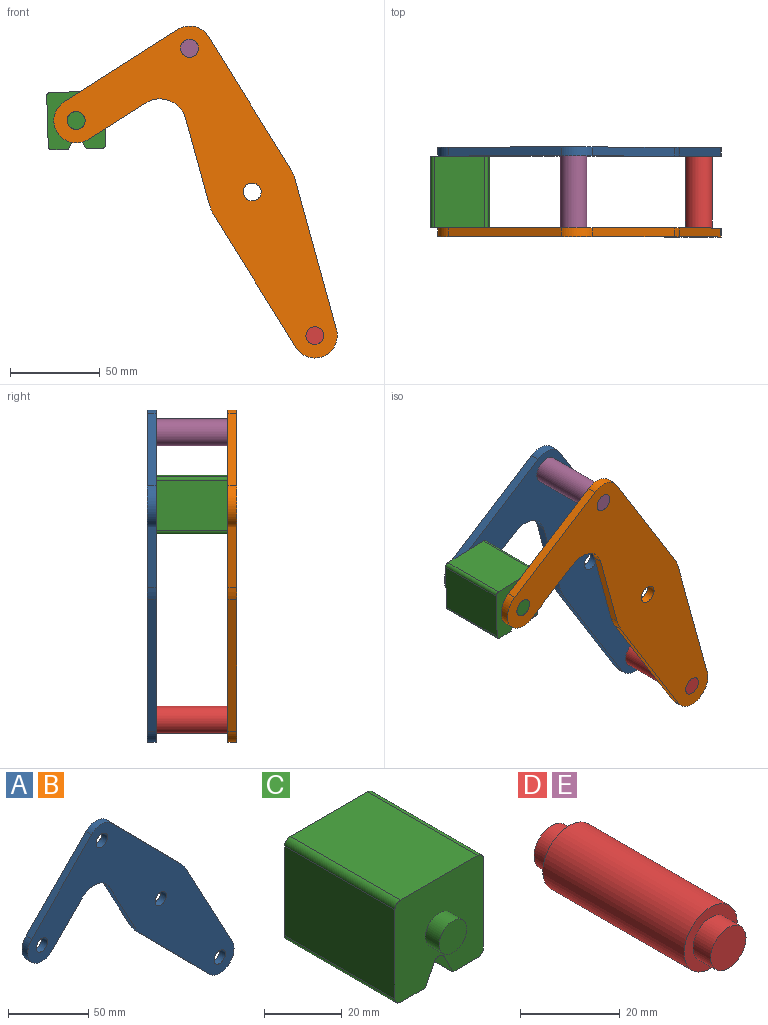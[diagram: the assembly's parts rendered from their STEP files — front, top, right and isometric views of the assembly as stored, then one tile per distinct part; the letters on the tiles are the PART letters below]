
ASSEMBLY  parts=5 mates=3
PART A: 18 faces, bbox 181.7x5x165.8 mm
  f0: plane 43.49x23.35mm, normal (-0.88,0,-0.47), area 246.8mm2, adj f1,f14,f16,f17
  f1: cylinder r=25mm len=5.75mm, axis (0,1,0), area 35.8mm2, adj f0,f2,f16,f17
  f2: plane 61.6x60.87mm, normal (-0.71,0,-0.7), area 433mm2, adj f1,f3,f16,f17
  f3: cylinder r=12.5mm len=21.39mm, axis (0,1,0), area 178.4mm2, adj f2,f4,f16,f17
  f4: plane 76.3x40.96mm, normal (0.88,0,0.47), area 433mm2, adj f3,f5,f16,f17
  f5: cylinder r=25mm len=5.75mm, axis (0,1,0), area 35.8mm2, adj f4,f6,f16,f17
  f6: plane 61.6x60.87mm, normal (0.71,0,0.7), area 433mm2, adj f5,f7,f16,f17
  f7: cylinder r=12.5mm len=17.78mm, axis (0,1,0), area 98.9mm2, adj f6,f8,f16,f17
  f8: plane 53.35x52.71mm, normal (-0.71,0,0.7), area 375mm2, adj f7,f9,f16,f17
  f9: cylinder r=12.5mm len=21.39mm, axis (0,1,0), area 196.3mm2, adj f8,f10,f16,f17
  f10: plane 26.86x26.54mm, normal (0.71,0,-0.7), area 188.8mm2, adj f9,f14,f16,f17
  f11: cylinder r=5mm len=10mm, axis (0,1,0), area 157.1mm2, adj f16,f17
  f12: cylinder r=5mm len=10mm, axis (0,1,0), area 157.1mm2, adj f16,f17
  f13: cylinder r=5mm len=10mm, axis (0,1,0), area 157.1mm2, adj f16,f17
  f14: cylinder r=15mm len=23.89mm, axis (0,1,0), area 140.2mm2, adj f0,f10,f16,f17
  f15: cylinder r=5mm len=10mm, axis (0,1,0), area 157.1mm2, adj f16,f17
  f16: plane 181.66x165.78mm, normal (0,-1,0), area 8710.1mm2, adj f0,f1,f2,f3,f4,f5,f6,f7
  f17: plane 181.66x165.78mm, normal (0,1,0), area 8710.1mm2, adj f0,f1,f2,f3,f4,f5,f6,f7
PART B: same geometry as A
PART C: 18 faces, bbox 32.1x50x32.1 mm
  f0: plane 40x28.08mm, normal (1,0,0), area 1123.1mm2, adj f4,f10,f13,f14
  f1: plane 40x9.04mm, normal (0,0,-1), area 361.6mm2, adj f2,f4,f10,f14
  f2: plane 40x6.42mm, normal (-0.89,0,-0.45), area 287.2mm2, adj f1,f4,f10,f15
  f3: plane 40x6.42mm, normal (0.89,0,-0.45), area 287.2mm2, adj f4,f5,f10,f15
  f4: plane 32.08x32.08mm, normal (0,-1,0), area 900.6mm2, adj f0,f1,f2,f3,f5,f6,f7,f9
  f5: plane 40x9.04mm, normal (0,0,-1), area 361.6mm2, adj f3,f4,f10,f16
  f6: plane 40x28.08mm, normal (0,0,1), area 1123.1mm2, adj f4,f10,f13,f17
  f7: plane 40x28.08mm, normal (-1,0,0), area 1123.1mm2, adj f4,f10,f16,f17
  f8: plane 10x10mm, normal (0,-1,0), area 78.5mm2, adj f9
  f9: cylinder r=5mm len=10mm, axis (0,1,0), area 157.1mm2, adj f4,f8
  f10: plane 32.08x32.08mm, normal (0,1,0), area 900.6mm2, adj f0,f1,f2,f3,f5,f6,f7,f12
  f11: plane 10x10mm, normal (0,1,0), area 78.5mm2, adj f12
  f12: cylinder r=5mm len=10mm, axis (0,-1,0), area 157.1mm2, adj f10,f11
  f13: cylinder r=2mm len=40mm, axis (0,1,0), area 125.7mm2, adj f0,f4,f6,f10
  f14: cylinder r=2mm len=40mm, axis (0,-1,0), area 125.7mm2, adj f0,f1,f4,f10
  f15: cylinder r=2mm len=40mm, axis (0,1,0), area 177.1mm2, adj f2,f3,f4,f10
  f16: cylinder r=2mm len=40mm, axis (0,1,0), area 125.7mm2, adj f4,f5,f7,f10
  f17: cylinder r=2mm len=40mm, axis (0,-1,0), area 125.7mm2, adj f4,f6,f7,f10
PART D: 7 faces, bbox 15x50x15 mm
  f0: cylinder r=7.5mm len=40mm, axis (0,-1,0), area 1885mm2, adj f2,f5
  f1: cylinder r=5mm len=10mm, axis (0,1,0), area 157.1mm2, adj f2,f3
  f2: plane 15x15mm, normal (0,-1,0), area 98.2mm2, adj f0,f1
  f3: plane 10x10mm, normal (0,-1,0), area 78.5mm2, adj f1
  f4: cylinder r=5mm len=10mm, axis (0,-1,0), area 157.1mm2, adj f5,f6
  f5: plane 15x15mm, normal (0,1,0), area 98.2mm2, adj f0,f4
  f6: plane 10x10mm, normal (0,1,0), area 78.5mm2, adj f4
PART E: same geometry as D
PLACE A rot(axis=(0,1,0),12.9deg) t=(0,25,0)mm
PLACE B rot(axis=(0,1,0),12.9deg) t=(0,-20,0)mm fixed
PLACE C rot(axis=(0,-1,0),1.7deg) t=(6.89,-20,26.07)mm
PLACE D rot(axis=(0,1,0),12.9deg) t=(70,-20,-160.39)mm
PLACE E rot(axis=(0,1,0),12.9deg) t=(0,-20,0)mm
MATE revolute C.f9 <-> B.f9  axis (0,-1,0) through (-98.27,-20,39.92)mm
MATE fastened A.f7 <-> E.f0  axis (0,-1,0) through (-35,20,80.2)mm
MATE fastened D.f0 <-> B.f3  axis (0,-1,0) through (35,-20,-80.2)mm
